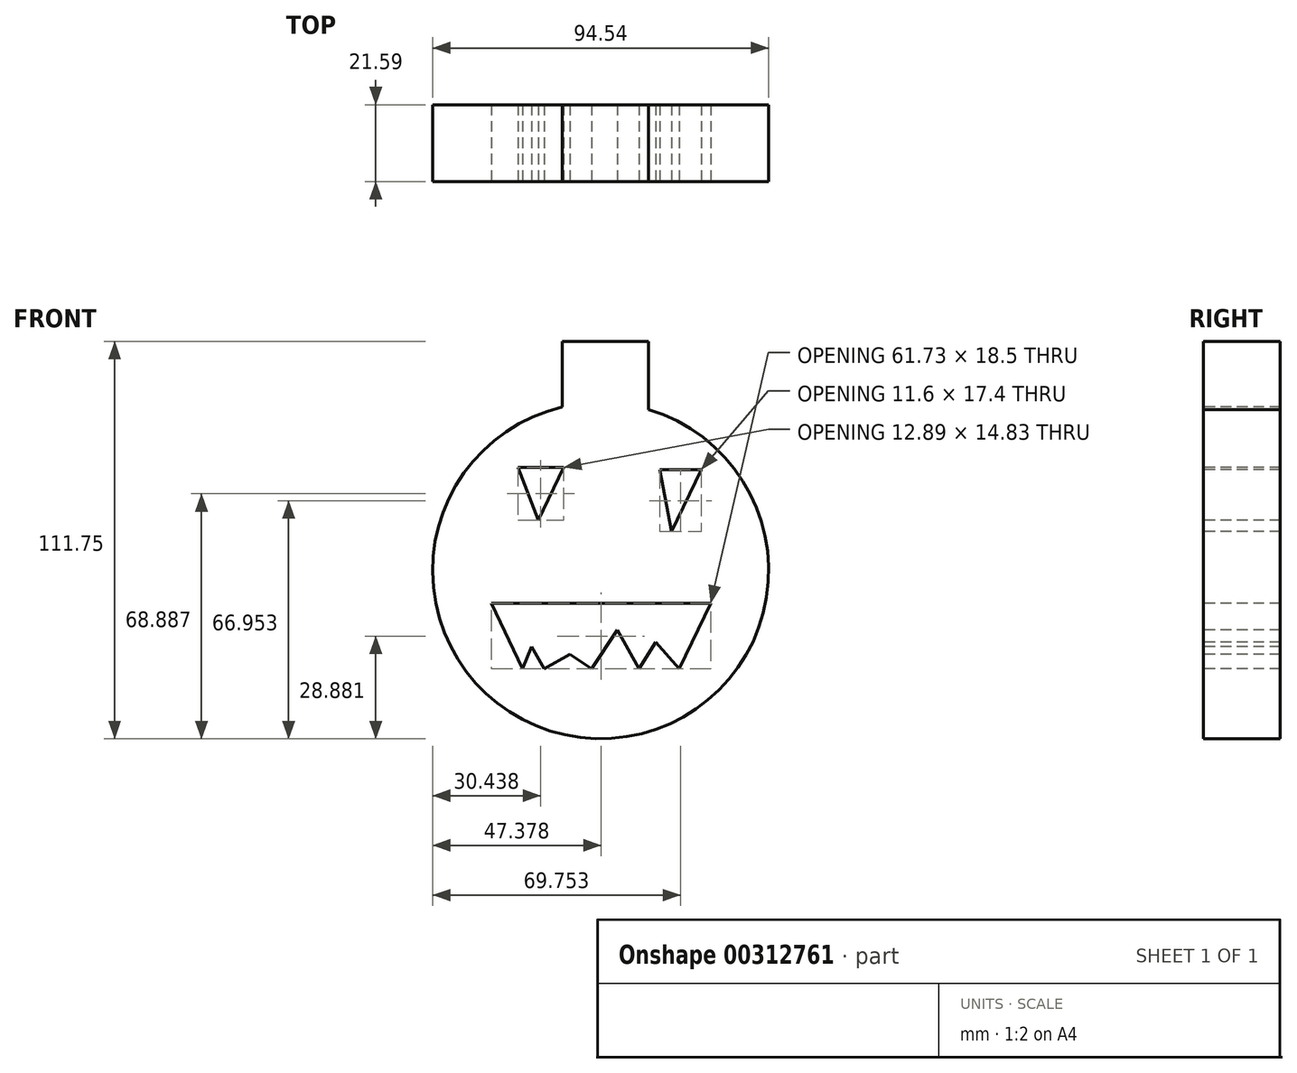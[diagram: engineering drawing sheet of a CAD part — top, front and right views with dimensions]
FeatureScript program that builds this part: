
annotation { "Feature Type Name" : "Feature", "Feature Type Description" : "" }
export const myFeature = defineFeature(function(context is Context, id is Id, definition is map)
    precondition{}
    {
        {
            var Q0;
            Q0=qCreatedBy(makeId("Front.planeOp"),FACE);
            var sketch = newSketch(context, id + "F0", { "sketchPlane" : qUnion([Q0])});
            skCircle(sketch, "E0", {"center": v(0, 0) * mm, "radius": 47.27 * mm});
            skLineSegment(sketch, "E1", {"start": v(-10.8, 46.02) * mm, "end": v(-10.8, 64.48) * mm});
            skLineSegment(sketch, "E2", {"start": v(-10.8, 64.48) * mm, "end": v(13.46, 64.48) * mm});
            skLineSegment(sketch, "E3", {"start": v(13.46, 64.48) * mm, "end": v(13.46, 45.3) * mm});
            skLineSegment(sketch, "E4", {"start": v(-23.28, 29.03) * mm, "end": v(-10.39, 29.03) * mm});
            skLineSegment(sketch, "E5", {"start": v(-10.39, 29.03) * mm, "end": v(-17.48, 14.2) * mm});
            skLineSegment(sketch, "E6", {"start": v(-17.48, 14.2) * mm, "end": v(-23.28, 29.03) * mm});
            skLineSegment(sketch, "E7", {"start": v(16.68, 28.39) * mm, "end": v(28.28, 28.39) * mm});
            skLineSegment(sketch, "E8", {"start": v(28.28, 28.39) * mm, "end": v(19.9, 10.98) * mm});
            skLineSegment(sketch, "E9", {"start": v(19.9, 10.98) * mm, "end": v(16.68, 28.39) * mm});
            skLineSegment(sketch, "E10", {"start": v(-20, 36.46) * mm, "end": v(-8.39, 30.43) * mm});
            skLineSegment(sketch, "E11", {"start": v(13.98, 31.5) * mm, "end": v(25.38, 36.67) * mm});
            skLineSegment(sketch, "E12", {"start": v(-30.76, -9.14) * mm, "end": v(30.97, -9.14) * mm});
            skLineSegment(sketch, "E13", {"start": v(30.97, -9.14) * mm, "end": v(22.15, -27.64) * mm});
            skLineSegment(sketch, "E14", {"start": v(22.15, -27.64) * mm, "end": v(15.49, -20.11) * mm});
            skLineSegment(sketch, "E15", {"start": v(15.49, -20.11) * mm, "end": v(10.75, -27.64) * mm});
            skLineSegment(sketch, "E16", {"start": v(10.75, -27.64) * mm, "end": v(4.73, -16.67) * mm});
            skLineSegment(sketch, "E17", {"start": v(4.73, -16.67) * mm, "end": v(-2.58, -27.64) * mm});
            skLineSegment(sketch, "E18", {"start": v(-2.58, -27.64) * mm, "end": v(-8.69, -23.57) * mm});
            skLineSegment(sketch, "E19", {"start": v(-8.69, -23.57) * mm, "end": v(-15.92, -27.64) * mm});
            skLineSegment(sketch, "E20", {"start": v(-15.92, -27.64) * mm, "end": v(-19.45, -21.36) * mm});
            skLineSegment(sketch, "E21", {"start": v(-19.45, -21.36) * mm, "end": v(-21.94, -27.64) * mm});
            skLineSegment(sketch, "E22", {"start": v(-30.76, -9.14) * mm, "end": v(-21.94, -27.64) * mm});
            skSolve(sketch);
        }
        {
            var Q0;
            Q0=makeQuery(id+"F0.imprint","IMPRINT",FACE,{"disambiguationData":[TD([[makeQuery(id+"F0.imprint","IMPRINT",EDGE,{"derivedFrom":sQuery(id+"F0.wireOp",EDGE,"E4")}),1.0]])]});
            var Q1;
            {var subQ0=sQuery(id+"F0.wireOp",EDGE,"E1");Q1=makeQuery(id+"F0.imprint","IMPRINT",FACE,{"disambiguationData":[TD([[makeQuery(id+"F0.imprint","IMPRINT",EDGE,{"derivedFrom":subQ0}),-1.0]])]});}
            extrude(context, id + "F1", {"entities" : qUnion([Q0, Q1]), "oppositeDirection" : true, "depth" : 21.59 * mm});
        }
    });
